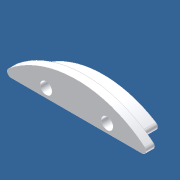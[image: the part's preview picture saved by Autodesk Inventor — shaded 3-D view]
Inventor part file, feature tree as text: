
AUTODESK INVENTOR PART (.ipt)
format: ipt  version: unknown  size: 201,216 bytes
history: native  units: in
note: dims shown in document units (in); Inventor stores cm internally (conversion verified against a paired STEP export)
features: sketch x3, extrude x2, fillet x2, hole x1
ambient origin geometry x8: Origin, YZ Plane, XZ Plane, XY Plane, X Axis, Y Axis, Z Axis, Center Point
bodies: Solid1 (feature_tree)
feature tree (8):
  extrude  "Extrusion1"  Depth=1.25in
  extrude  "Extrusion2"  Depth=0.145in
  hole  "Hole1"  [1 undecoded]
  fillet  "Fillet1"  Radius=0.5in
  fillet  "Fillet2"  Radius=0.1406in
  sketch  "Sketch1"  dims[d0=3.2269in d1=1.25in]
  sketch  "Sketch2"  dims[d2=0.3in d3=0.0in d4=0.145in]
  sketch  "Sketch3"  dims[d5=0.1375in d6=0.0in d7=0.5in d8=0.5in d9=0.1406in d10=0.1406in d11=0.196in d12=0.75in d13=0.385in d14=0.25in d15=0.5635in d16=1.0in d17=0.8108in d18=0.0625in d19=0.0625in]
note: 1 required parameter value undecoded (feature->parameter linkage not recoverable at this tier; creation-order binding heuristic only, values carry confidence <= 0.55)
